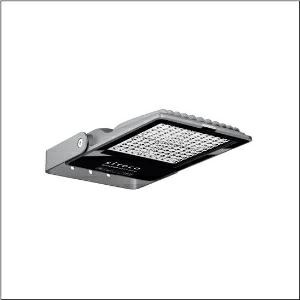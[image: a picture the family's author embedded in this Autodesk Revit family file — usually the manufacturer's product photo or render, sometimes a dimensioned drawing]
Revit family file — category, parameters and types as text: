
# Revit family: sicompact_r__31_mini___pl32_5xa7571c2k23_606d
name_source: partatom
category: Lighting Fixtures
units: mm (PartAtom-declared; Revit-internal decimal feet)

## family parameters
Cut with Voids When Loaded = No
Host = Face
Light Source = No
Part Type = Normal
Room Calculation Point = No
Round Connector Dimension = Use Diameter
Shared = No

## types (1)
- SiCompact® 31 mini  PL32 (1 x LED, 15000 lm, 95 W, 4000K)
    Apparent Load = 95 VA
    CIE Flux Codes = 32 69 98 100 100
    Color Rendering = 70
    Color Temperature = 4000K
    Default Elevation = 1800 mm
    Description = SiCompact® 31 mini, floodlight, primary light control with lens, of plastic, of toughened safety glass, transparent, light distribution: PL32, light emission: direct distribution, primary light characteristic: asymmetric, installation type: surface-mounted, LED, High Power LED, rated luminous flux: 15.000lm, luminous efficacy: 158lm/W, light colour: 740, colour temperature: 4000K, control gear: ECG, with cable, 3x 1.5mm², mains connection: 220..240V, AC, 50/60Hz, connection cable pre-assembled, cable length: 2m, rated input power: 95W, of diecast aluminium, specular, metallic grey (RAL 9006), length: 461mm, width: 261mm, height: 62mm, bracket, of sheet steel, coated, metallic grey (RAL 9006), ON/OFF, protection rating (complete): IP66, insulation class (complete): insulation class I (protective earthing), certification: CE, ENEC, impact resistance: IK08, permissible operating ambient temperature: -40..+45°C, packaging unit: 1 piece

Light Distribution: PL32
    Height = 62 mm  [stored 0.203412 ft]
    Lamp = 1 x LED
    Lamp Light Flux = 15000 lm
    Lamp Power = 95 W
    Lamp count = 1
    Length = 460 mm
    Luminous efficacy = 158 lm/W
    Manufacturer = Siteco
    ModVariant = No
    Model = 5XA7571C2K23
    Mounting Place = Wall
    Mounting Type = Surface mounted
    Number of Poles = 1
    OnlyDefault = Yes
    Power Factor = 1
    Product Name = SiCompact® 31 mini | PL32
    Product group = floodlight | wall mounted
    ProductGroupID = 2001
    Protection Class = Protection class I
    Protection Degree = IP 66
    RLX_Detail_Level = 1
    RLX_Emergency_Light_Flux = 0 lm
    RLX_Emergency_Type = 0
    RLX_Emergency_Type_DB = No
    RlxData = <blob elided: 126921 chars, md5=b6c825ce>
    Socket = socket
    Standby Power = 0 W
    System Light Flux = 15000 lm
    System Power = 95 W
    Type Comments = Product without accessories
    Type Image = l_1006951.jpg
    URL = http://relux.com
    VarID = ---
    Voltage = 0 V
    Weight = 0.00 kg
    Width = 260 mm

note: [stored X ft] marks values corroborated as IEEE doubles in the binary element streams (Revit-internal decimal feet)

## geometry (parser evidence)
native form markers: Blend x4, Sweep x14
no freeform markers — native parametric forms only
